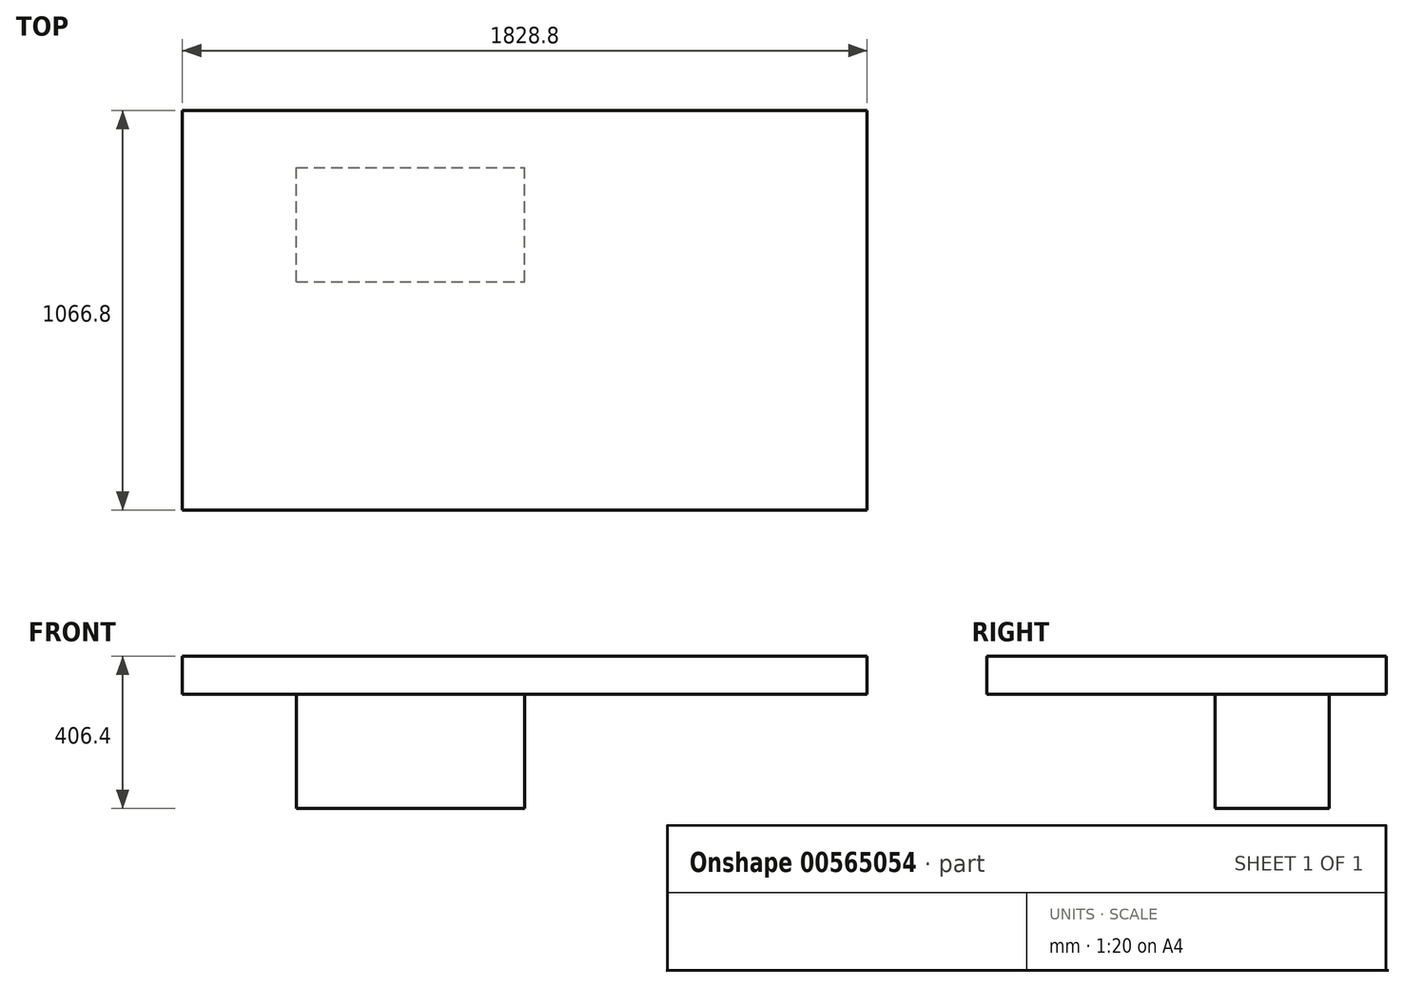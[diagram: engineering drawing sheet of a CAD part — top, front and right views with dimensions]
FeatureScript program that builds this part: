
annotation { "Feature Type Name" : "Feature", "Feature Type Description" : "" }
export const myFeature = defineFeature(function(context is Context, id is Id, definition is map)
    precondition{}
    {
        {
            var Q0;
            Q0=qCreatedBy(makeId("Top.planeOp"),FACE);
            var sketch = newSketch(context, id + "F0", { "sketchPlane" : qUnion([Q0])});
            skLineSegment(sketch, "E0.bottom", {"start": v(0, 0) * mm, "end": v(1828.8, 0) * mm});
            skLineSegment(sketch, "E0.top", {"start": v(0, -1066.8) * mm, "end": v(1828.8, -1066.8) * mm});
            skLineSegment(sketch, "E0.left", {"start": v(0, 0) * mm, "end": v(0, -1066.8) * mm});
            skLineSegment(sketch, "E0.right", {"start": v(1828.8, 0) * mm, "end": v(1828.8, -1066.8) * mm});
            skSolve(sketch);
        }
        {
            var Q0;
            Q0=makeQuery(id+"F0.imprint","IMPRINT",FACE,{"disambiguationData":[TD([[makeQuery(id+"F0.imprint","IMPRINT",EDGE,{"derivedFrom":sQuery(id+"F0.wireOp",EDGE,"E0.bottom")}),-1.0]])]});
            extrude(context, id + "F1", {"entities" : qUnion([Q0]), "depth" : 101.6 * mm, "offsetDistance" : 25.4 * mm});
        }
        {
            var Q0;
            Q0=makeQuery(id+"F1.opExtrude","CAP_FACE",FACE,{"disambiguationData":[OSD([sQuery(id+"F0.wireOp",EDGE,"E0.bottom"),sQuery(id+"F0.wireOp",EDGE,"E0.top"),sQuery(id+"F0.wireOp",EDGE,"E0.left"),sQuery(id+"F0.wireOp",EDGE,"E0.right")])],"isStart":true});
            var sketch = newSketch(context, id + "F2", { "sketchPlane" : qUnion([Q0])});
            skLineSegment(sketch, "E1", {"start": v(0, 0) * mm, "end": v(0, 152.4) * mm, "construction": true});
            skLineSegment(sketch, "E2", {"start": v(0, 152.4) * mm, "end": v(304.8, 152.4) * mm, "construction": true});
            skLineSegment(sketch, "E3", {"start": v(304.8, 152.4) * mm, "end": v(304.8, 457.2) * mm, "construction": true});
            skLineSegment(sketch, "E4.bottom", {"start": v(304.8, 457.2) * mm, "end": v(914.4, 457.2) * mm});
            skLineSegment(sketch, "E4.top", {"start": v(304.8, 152.4) * mm, "end": v(914.4, 152.4) * mm});
            skLineSegment(sketch, "E4.left", {"start": v(304.8, 457.2) * mm, "end": v(304.8, 152.4) * mm});
            skLineSegment(sketch, "E4.right", {"start": v(914.4, 457.2) * mm, "end": v(914.4, 152.4) * mm});
            skSolve(sketch);
        }
        {
            var Q0;
            Q0=makeQuery(id+"F2.imprint","IMPRINT",FACE,{"disambiguationData":[TD([[makeQuery(id+"F2.imprint","IMPRINT",EDGE,{"derivedFrom":sQuery(id+"F2.wireOp",EDGE,"E4.bottom")}),-1.0]])]});
            extrude(context, id + "F3", {"entities" : qUnion([Q0]), "operationType" : NewBodyOperationType.ADD, "depth" : 304.8 * mm, "offsetDistance" : 25.4 * mm});
        }
    });
